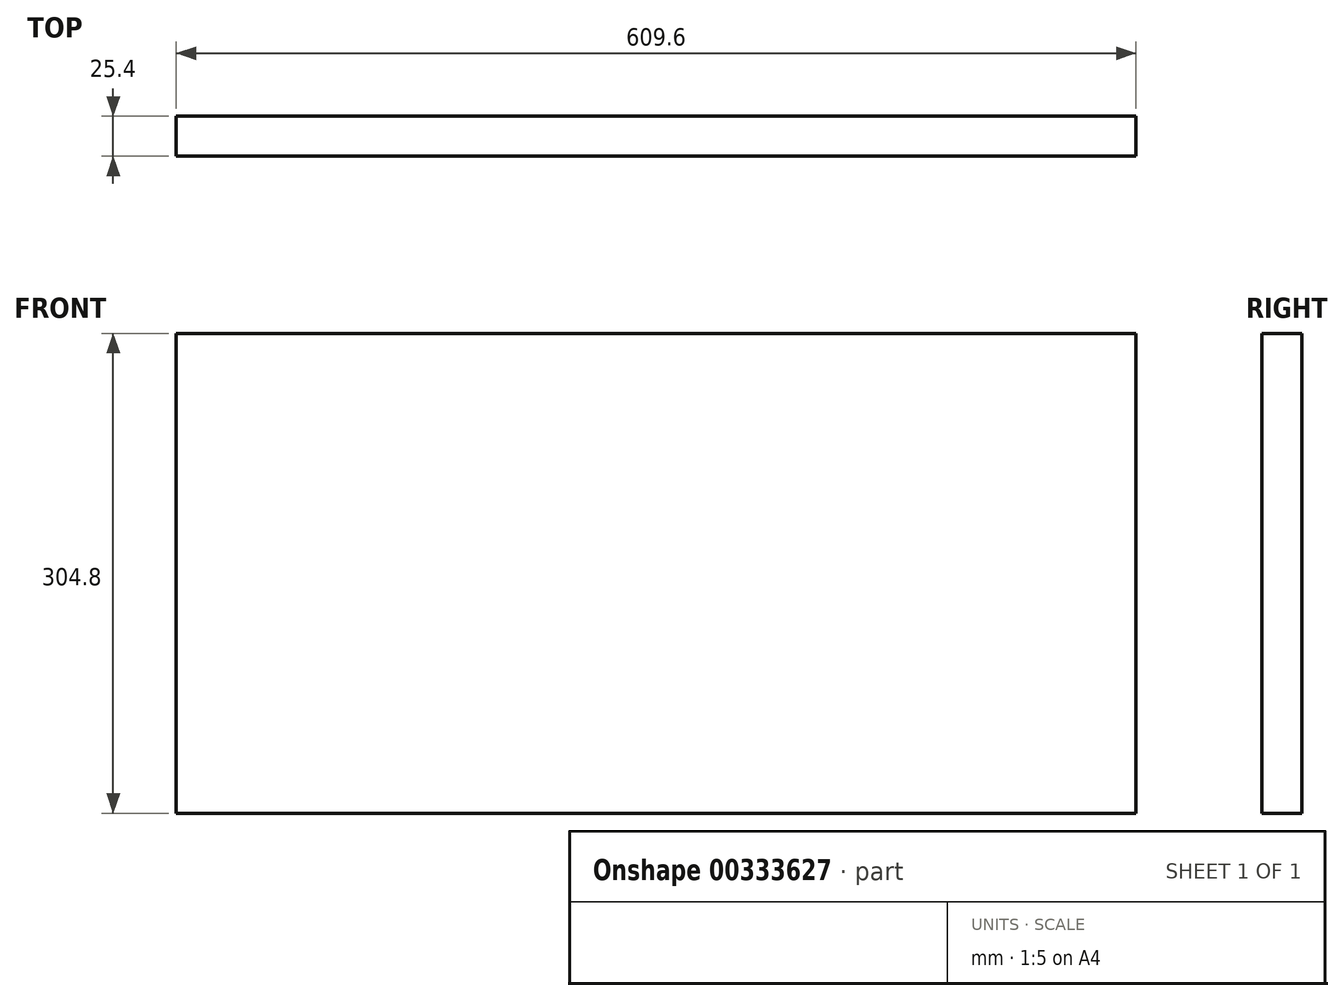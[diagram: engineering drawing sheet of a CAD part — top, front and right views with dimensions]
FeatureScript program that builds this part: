
annotation { "Feature Type Name" : "Feature", "Feature Type Description" : "" }
export const myFeature = defineFeature(function(context is Context, id is Id, definition is map)
    precondition{}
    {
        {
            var Q0;
            Q0=qCreatedBy(makeId("Front.planeOp"),FACE);
            var sketch = newSketch(context, id + "F0", { "sketchPlane" : qUnion([Q0])});
            skLineSegment(sketch, "E0.bottom", {"start": v(-304.91, 94.5) * mm, "end": v(304.69, 94.5) * mm});
            skLineSegment(sketch, "E0.top", {"start": v(-304.91, -210.3) * mm, "end": v(304.69, -210.3) * mm});
            skLineSegment(sketch, "E0.left", {"start": v(-304.91, 94.5) * mm, "end": v(-304.91, -210.3) * mm});
            skLineSegment(sketch, "E0.right", {"start": v(304.69, 94.5) * mm, "end": v(304.69, -210.3) * mm});
            skSolve(sketch);
        }
        {
            var Q0;
            Q0=makeQuery(id+"F0.imprint","IMPRINT",FACE,{"disambiguationData":[TD([[makeQuery(id+"F0.imprint","IMPRINT",EDGE,{"derivedFrom":sQuery(id+"F0.wireOp",EDGE,"E0.bottom")}),-1.0]])]});
            extrude(context, id + "F1", {"entities" : qUnion([Q0]), "depth" : 25.4 * mm});
        }
    });
